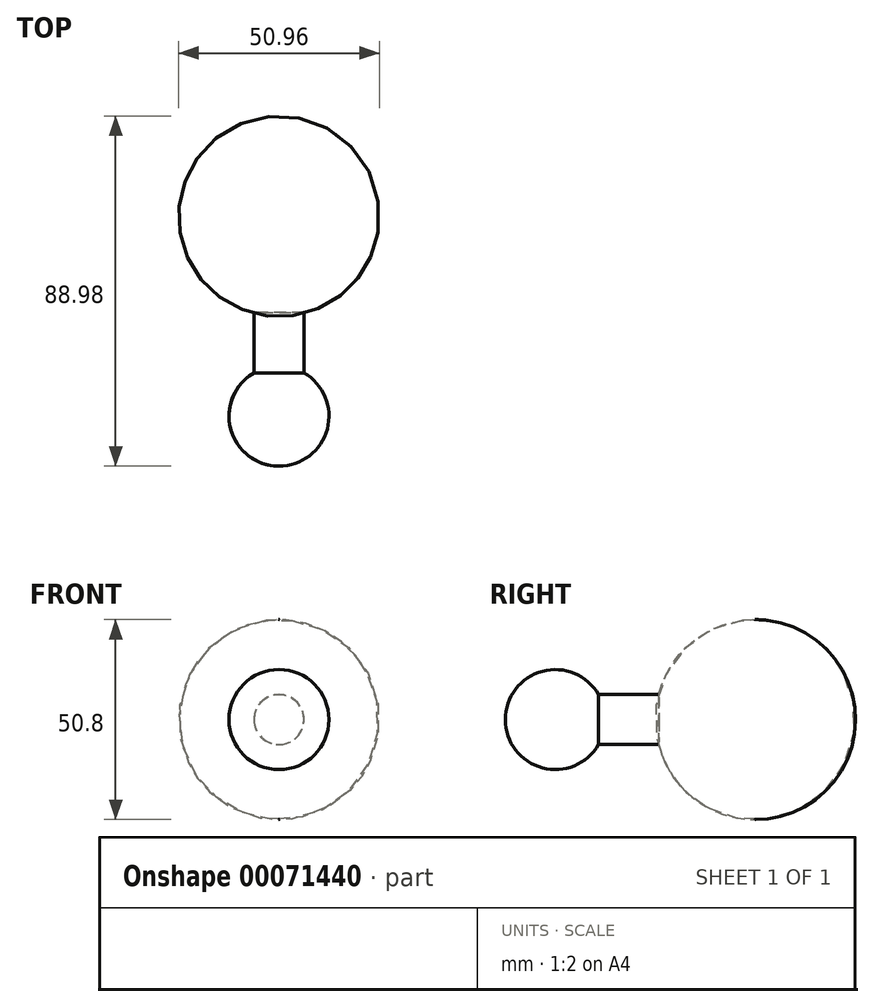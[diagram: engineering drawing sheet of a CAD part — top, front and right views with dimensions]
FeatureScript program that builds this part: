
annotation { "Feature Type Name" : "Feature", "Feature Type Description" : "" }
export const myFeature = defineFeature(function(context is Context, id is Id, definition is map)
    precondition{}
    {
        {
            var Q0;
            Q0=qCreatedBy(makeId("Front.planeOp"),FACE);
            var sketch = newSketch(context, id + "F0", { "sketchPlane" : qUnion([Q0])});
            skLineSegment(sketch, "E0", {"start": v(0, -25.4) * mm, "end": v(0, 25.4) * mm});
            skArc(sketch, "E1", {"start": v(0, 25.4) * mm, "mid": v(-25.32, 0) * mm, "end": v(0, -25.4) * mm});
            skSolve(sketch);
        }
        {
            var Q0;
            Q0=makeQuery(id+"F0.imprint","IMPRINT",FACE,{"disambiguationData":[TD([[makeQuery(id+"F0.imprint","IMPRINT",EDGE,{"derivedFrom":sQuery(id+"F0.wireOp",EDGE,"E0")}),1.0]])]});
            var Q1;
            Q1=sQuery(id+"F0.wireOp",EDGE,"E0");
            revolve(context, id + "F1", {"entities" : qUnion([Q0]), "axis" : qUnion([Q1]), "revolveType" : RevolveType.FULL});
        }
        {
            var Q0;
            Q0=qCreatedBy(makeId("Front.planeOp"),FACE);
            var sketch = newSketch(context, id + "F2", { "sketchPlane" : qUnion([Q0])});
            skCircle(sketch, "E2", {"center": v(0, 0) * mm, "radius": 6.35 * mm});
            skSolve(sketch);
        }
        {
            var Q0;
            Q0 = qSketchRegion(id + "F2", true);
            extrude(context, id + "F3", {"entities" : qUnion([Q0]), "operationType" : NewBodyOperationType.ADD, "depth" : 50.8 * mm});
        }
        {
            var Q0;
            Q0=qCreatedBy(makeId("Top.planeOp"),FACE);
            var sketch = newSketch(context, id + "F4", { "sketchPlane" : qUnion([Q0])});
            skLineSegment(sketch, "E3", {"start": v(0, -38.1) * mm, "end": v(0, -63.5) * mm});
            skArc(sketch, "E4", {"start": v(0, -38.1) * mm, "mid": v(-12.7, -50.8) * mm, "end": v(0, -63.5) * mm});
            skSolve(sketch);
        }
        {
            var Q0;
            Q0=makeQuery(id+"F4.imprint","IMPRINT",FACE,{"disambiguationData":[TD([[makeQuery(id+"F4.imprint","IMPRINT",EDGE,{"derivedFrom":sQuery(id+"F4.wireOp",EDGE,"E3")}),-1.0]])]});
            var Q1;
            Q1=sQuery(id+"F4.wireOp",EDGE,"E3");
            revolve(context, id + "F5", {"operationType" : NewBodyOperationType.ADD, "entities" : qUnion([Q0]), "axis" : qUnion([Q1]), "revolveType" : RevolveType.FULL});
        }
    });
